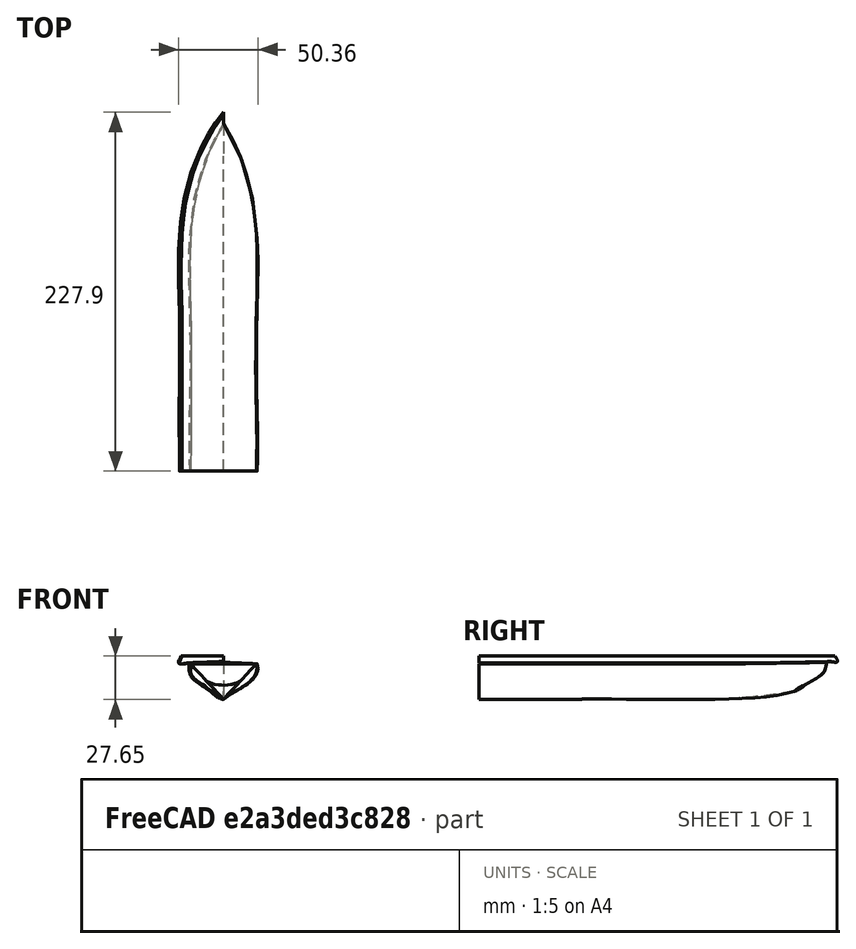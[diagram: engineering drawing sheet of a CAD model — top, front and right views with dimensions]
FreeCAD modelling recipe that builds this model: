
FCSTD DOCUMENT  (FreeCAD 0.21R33771 (Git))
Label: ship drg.
License: All rights reserved
LicenseURL: http://en.wikipedia.org/wiki/All_rights_reserved
objects: Part::FeaturePython×12, App::DocumentObjectGroup×5, Sketcher::SketchObject×4, Part::RuledSurface×3, Part::Loft×2, Part::Mirroring×2, Part::Part2DObjectPython×1, Part::Compound×1
note: 25 computed .brp shape members not serialized (recipe doc carries the construction recipe); baked Part::Feature solids carry a one-line shape summary decoded from their .brp

FEATURE [Sketcher::SketchObject] Sketch
  FullyConstrained = false
  Placement = pos=(0,0,0) rot=(1,0,0;1.5708rad)
  sketch-geometry (14):
    g0: LineSegment StartX=0 StartY=10 StartZ=0 EndX=0 EndY=15.6184 EndZ=0
    g1: LineSegment StartX=0 StartY=15.6184 StartZ=0 EndX=0 EndY=21.2368 EndZ=0
    g2: LineSegment StartX=0 StartY=21.2368 StartZ=0 EndX=0 EndY=26.8551 EndZ=0
    g3: LineSegment StartX=0 StartY=26.8551 StartZ=0 EndX=0 EndY=32.4735 EndZ=0
    g4: LineSegment StartX=0 StartY=32.4735 StartZ=0 EndX=0 EndY=38.0919 EndZ=0
    g5: LineSegment StartX=0 StartY=10 StartZ=0 EndX=0 EndY=0 EndZ=0
    g6: LineSegment StartX=0 StartY=15.6184 StartZ=0 EndX=8.31751 EndY=15.6184 EndZ=0
    g7: LineSegment StartX=0 StartY=21.2368 StartZ=0 EndX=16.635 EndY=21.2368 EndZ=0
    g8: LineSegment StartX=0 StartY=26.8551 StartZ=0 EndX=20.7934 EndY=26.8551 EndZ=0
    g9: LineSegment StartX=0 StartY=32.4735 StartZ=0 EndX=20.9422 EndY=32.4735 EndZ=0
    g10: LineSegment StartX=0 StartY=10 StartZ=0 EndX=16.635 EndY=21.2368 EndZ=0
    g11: Circle CenterX=10.7614 CenterY=29.9321 CenterZ=0 NormalX=0 NormalY=0 NormalZ=1 AngleXU=0 Radius=10.4932
    g12: LineSegment StartX=20.9422 StartY=32.4735 StartZ=0 EndX=26.3293 EndY=32.4735 EndZ=0
    g13: LineSegment StartX=26.3293 StartY=32.4735 StartZ=0 EndX=26.3293 EndY=37.3944 EndZ=0
  constraints (36):
    c: PointOnObject(g0,g-2)
    c: PointOnObject(g0,g-2)
    c: Coincident(g0,g1)
    c: PointOnObject(g1,g-2)
    c: Coincident(g1,g2)
    c: PointOnObject(g2,g-2)
    c: Coincident(g2,g3)
    c: PointOnObject(g3,g-2)
    c: Coincident(g3,g4)
    c: PointOnObject(g4,g-2)
    c: Equal(g4,g3)
    c: Equal(g3,g2)
    c: Equal(g2,g1)
    c: Equal(g1,g0)
    c: Coincident(g5,g0)
    c: Coincident(g5,g-1)
    c: DistanceY(g5,g5) = 10
    c: Coincident(g6,g0)
    c: Horizontal(g6)
    c: Coincident(g7,g1)
    c: Horizontal(g7)
    c: Coincident(g8,g2)
    c: Horizontal(g8)
    c: Coincident(g9,g3)
    c: Horizontal(g9)
    c: Coincident(g10,g0)
    c: Coincident(g10,g7)
    c: PointOnObject(g6,g10)
    c: PointOnObject(g7,g11)
    c: PointOnObject(g8,g11)
    c: PointOnObject(g9,g11)
    c: Tangent(g10,g11)
    c: Coincident(g12,g9)
    c: Horizontal(g12)
    c: Coincident(g13,g12)
    c: Vertical(g13)
FEATURE [Part::FeaturePython] Interpolation_Curve  # WARN: FeaturePython — macro-defined, semantics opaque (R4)
  CustomTangents = false
  DetectAligned = false
  Parameters = [0,0.171956,0.385813,0.692906,1]
  Parametrization = 0
  Periodic = false
  PointList = -> [Sketch]
  Polygonal = false
  StartOffset = 0
  Tangents = (5) [(0.285541,2.128e-16,-0.958366),(-0.349691,2.08026e-16,-0.936865),(-0.74239,1.48763e-16,-0.669969),(-0.866574,1.10811e-16,-0.499049),(-0.736883,1.50107e-16,-0.67602)]
  Tolerance = 1e-07
  UTurns = 0
  VTurns = 0
  WireOutput = false
FEATURE [App::DocumentObjectGroup] Group  label="section1"
  Group = -> [Sketch,Interpolation_Curve]
FEATURE [Sketcher::SketchObject] Sketch001
  FullyConstrained = false
  Placement = pos=(0,50,0) rot=(1,0,0;1.5708rad)
  sketch-geometry (14):
    g0: LineSegment StartX=0 StartY=10 StartZ=0 EndX=0 EndY=15.6184 EndZ=0
    g1: LineSegment StartX=0 StartY=15.6184 StartZ=0 EndX=0 EndY=21.2368 EndZ=0
    g2: LineSegment StartX=0 StartY=21.2368 StartZ=0 EndX=0 EndY=26.8551 EndZ=0
    g3: LineSegment StartX=0 StartY=26.8551 StartZ=0 EndX=0 EndY=32.4735 EndZ=0
    g4: LineSegment StartX=0 StartY=32.4735 StartZ=0 EndX=0 EndY=38.0919 EndZ=0
    g5: LineSegment StartX=0 StartY=10 StartZ=0 EndX=0 EndY=0 EndZ=0
    g6: LineSegment StartX=0 StartY=15.6184 StartZ=0 EndX=8.2623 EndY=15.6184 EndZ=0
    g7: LineSegment StartX=0 StartY=21.2368 StartZ=0 EndX=16.5246 EndY=21.2368 EndZ=0
    g8: LineSegment StartX=0 StartY=26.8551 StartZ=0 EndX=20.6246 EndY=26.8551 EndZ=0
    g9: LineSegment StartX=0 StartY=32.4735 StartZ=0 EndX=20.6915 EndY=32.4735 EndZ=0
    g10: LineSegment StartX=0 StartY=10 StartZ=0 EndX=16.5246 EndY=21.2368 EndZ=0
    g11: Circle CenterX=10.7133 CenterY=29.7827 CenterZ=0 NormalX=0 NormalY=0 NormalZ=1 AngleXU=0 Radius=10.3347
    g12: LineSegment StartX=20.6915 StartY=32.4735 StartZ=0 EndX=26.3293 EndY=32.4735 EndZ=0
    g13: LineSegment StartX=26.3293 StartY=32.4735 StartZ=0 EndX=26.3293 EndY=37.3944 EndZ=0
  constraints (36):
    c: PointOnObject(g0,g-2)
    c: PointOnObject(g0,g-2)
    c: Coincident(g0,g1)
    c: PointOnObject(g1,g-2)
    c: Coincident(g1,g2)
    c: PointOnObject(g2,g-2)
    c: Coincident(g2,g3)
    c: PointOnObject(g3,g-2)
    c: Coincident(g3,g4)
    c: PointOnObject(g4,g-2)
    c: Equal(g4,g3)
    c: Equal(g3,g2)
    c: Equal(g2,g1)
    c: Equal(g1,g0)
    c: Coincident(g5,g0)
    c: Coincident(g5,g-1)
    c: DistanceY(g5,g5) = 10
    c: Coincident(g6,g0)
    c: Horizontal(g6)
    c: Coincident(g7,g1)
    c: Horizontal(g7)
    c: Coincident(g8,g2)
    c: Horizontal(g8)
    c: Coincident(g9,g3)
    c: Horizontal(g9)
    c: Coincident(g10,g0)
    c: Coincident(g10,g7)
    c: PointOnObject(g6,g10)
    c: PointOnObject(g7,g11)
    c: PointOnObject(g8,g11)
    c: PointOnObject(g9,g11)
    c: Tangent(g10,g11)
    c: Coincident(g12,g9)
    c: Horizontal(g12)
    c: Coincident(g13,g12)
    c: Vertical(g13)
FEATURE [Part::FeaturePython] Interpolation_Curve001  # WARN: FeaturePython — macro-defined, semantics opaque (R4)
  CustomTangents = false
  DetectAligned = false
  Parameters = [0,0.172581,0.386214,0.693107,1]
  Parametrization = 0
  Periodic = false
  PointList = -> [Sketch001]
  Polygonal = false
  StartOffset = 0
  Tangents = (5) [(0.285541,2.128e-16,-0.958366),(-0.349691,2.08026e-16,-0.936865),(-0.74239,1.48763e-16,-0.669969),(-0.866574,1.10811e-16,-0.499049),(-0.736883,1.50107e-16,-0.67602)]
  Tolerance = 1e-07
  UTurns = 0
  VTurns = 0
  WireOutput = false
FEATURE [App::DocumentObjectGroup] Group001  label="section002"
  Group = -> [Sketch001,Interpolation_Curve001]
FEATURE [Sketcher::SketchObject] Sketch002
  FullyConstrained = false
  Placement = pos=(0,100,0) rot=(1,0,0;1.5708rad)
  sketch-geometry (14):
    g0: LineSegment StartX=0 StartY=10 StartZ=0 EndX=0 EndY=15.6184 EndZ=0
    g1: LineSegment StartX=0 StartY=15.6184 StartZ=0 EndX=0 EndY=21.2368 EndZ=0
    g2: LineSegment StartX=0 StartY=21.2368 StartZ=0 EndX=0 EndY=26.8551 EndZ=0
    g3: LineSegment StartX=0 StartY=26.8551 StartZ=0 EndX=0 EndY=32.4735 EndZ=0
    g4: LineSegment StartX=0 StartY=32.4735 StartZ=0 EndX=0 EndY=38.0919 EndZ=0
    g5: LineSegment StartX=0 StartY=10 StartZ=0 EndX=0 EndY=0 EndZ=0
    g6: LineSegment StartX=0 StartY=15.6184 StartZ=0 EndX=8.31751 EndY=15.6184 EndZ=0
    g7: LineSegment StartX=0 StartY=21.2368 StartZ=0 EndX=16.635 EndY=21.2368 EndZ=0
    g8: LineSegment StartX=0 StartY=26.8551 StartZ=0 EndX=20.7934 EndY=26.8551 EndZ=0
    g9: LineSegment StartX=0 StartY=32.4735 StartZ=0 EndX=20.9422 EndY=32.4735 EndZ=0
    g10: LineSegment StartX=0 StartY=10 StartZ=0 EndX=16.635 EndY=21.2368 EndZ=0
    g11: Circle CenterX=10.7614 CenterY=29.9321 CenterZ=0 NormalX=0 NormalY=0 NormalZ=1 AngleXU=0 Radius=10.4932
    g12: LineSegment StartX=20.9422 StartY=32.4735 StartZ=0 EndX=26.3293 EndY=32.4735 EndZ=0
    g13: LineSegment StartX=26.3293 StartY=32.4735 StartZ=0 EndX=26.3293 EndY=37.3944 EndZ=0
  constraints (36):
    c: PointOnObject(g0,g-2)
    c: PointOnObject(g0,g-2)
    c: Coincident(g0,g1)
    c: PointOnObject(g1,g-2)
    c: Coincident(g1,g2)
    c: PointOnObject(g2,g-2)
    c: Coincident(g2,g3)
    c: PointOnObject(g3,g-2)
    c: Coincident(g3,g4)
    c: PointOnObject(g4,g-2)
    c: Equal(g4,g3)
    c: Equal(g3,g2)
    c: Equal(g2,g1)
    c: Equal(g1,g0)
    c: Coincident(g5,g0)
    c: Coincident(g5,g-1)
    c: DistanceY(g5,g5) = 10
    c: Coincident(g6,g0)
    c: Horizontal(g6)
    c: Coincident(g7,g1)
    c: Horizontal(g7)
    c: Coincident(g8,g2)
    c: Horizontal(g8)
    c: Coincident(g9,g3)
    c: Horizontal(g9)
    c: Coincident(g10,g0)
    c: Coincident(g10,g7)
    c: PointOnObject(g6,g10)
    c: PointOnObject(g7,g11)
    c: PointOnObject(g8,g11)
    c: PointOnObject(g9,g11)
    c: Tangent(g10,g11)
    c: Coincident(g12,g9)
    c: Horizontal(g12)
    c: Coincident(g13,g12)
    c: Vertical(g13)
FEATURE [Part::FeaturePython] Interpolation_Curve002  # WARN: FeaturePython — macro-defined, semantics opaque (R4)
  CustomTangents = false
  DetectAligned = false
  Parameters = [0,0.171956,0.385813,0.692906,1]
  Parametrization = 0
  Periodic = false
  PointList = -> [Sketch002]
  Polygonal = false
  StartOffset = 0
  Tangents = (5) [(0.285541,2.128e-16,-0.958366),(-0.349691,2.08026e-16,-0.936865),(-0.74239,1.48763e-16,-0.669969),(-0.866574,1.10811e-16,-0.499049),(-0.736883,1.50107e-16,-0.67602)]
  Tolerance = 1e-07
  UTurns = 0
  VTurns = 0
  WireOutput = false
FEATURE [App::DocumentObjectGroup] Group002  label="section003"
  Group = -> [Sketch002,Interpolation_Curve002]
FEATURE [Sketcher::SketchObject] Sketch003
  FullyConstrained = false
  Placement = pos=(0,150,0) rot=(1,0,0;1.5708rad)
  sketch-geometry (14):
    g0: LineSegment StartX=0 StartY=10 StartZ=0 EndX=0 EndY=15.6184 EndZ=0
    g1: LineSegment StartX=0 StartY=15.6184 StartZ=0 EndX=0 EndY=21.2368 EndZ=0
    g2: LineSegment StartX=0 StartY=21.2368 StartZ=0 EndX=0 EndY=26.8551 EndZ=0
    g3: LineSegment StartX=0 StartY=26.8551 StartZ=0 EndX=0 EndY=32.4735 EndZ=0
    g4: LineSegment StartX=0 StartY=32.4735 StartZ=0 EndX=0 EndY=38.0919 EndZ=0
    g5: LineSegment StartX=0 StartY=10 StartZ=0 EndX=0 EndY=0 EndZ=0
    g6: LineSegment StartX=0 StartY=15.6184 StartZ=0 EndX=8.31751 EndY=15.6184 EndZ=0
    g7: LineSegment StartX=0 StartY=21.2368 StartZ=0 EndX=16.635 EndY=21.2368 EndZ=0
    g8: LineSegment StartX=0 StartY=26.8551 StartZ=0 EndX=20.7934 EndY=26.8551 EndZ=0
    g9: LineSegment StartX=0 StartY=32.4735 StartZ=0 EndX=20.9422 EndY=32.4735 EndZ=0
    g10: LineSegment StartX=0 StartY=10 StartZ=0 EndX=16.635 EndY=21.2368 EndZ=0
    g11: Circle CenterX=10.7614 CenterY=29.9321 CenterZ=0 NormalX=0 NormalY=0 NormalZ=1 AngleXU=0 Radius=10.4932
    g12: LineSegment StartX=20.9422 StartY=32.4735 StartZ=0 EndX=26.3293 EndY=32.4735 EndZ=0
    g13: LineSegment StartX=26.3293 StartY=32.4735 StartZ=0 EndX=26.3293 EndY=37.3944 EndZ=0
  constraints (36):
    c: PointOnObject(g0,g-2)
    c: PointOnObject(g0,g-2)
    c: Coincident(g0,g1)
    c: PointOnObject(g1,g-2)
    c: Coincident(g1,g2)
    c: PointOnObject(g2,g-2)
    c: Coincident(g2,g3)
    c: PointOnObject(g3,g-2)
    c: Coincident(g3,g4)
    c: PointOnObject(g4,g-2)
    c: Equal(g4,g3)
    c: Equal(g3,g2)
    c: Equal(g2,g1)
    c: Equal(g1,g0)
    c: Coincident(g5,g0)
    c: Coincident(g5,g-1)
    c: DistanceY(g5,g5) = 10
    c: Coincident(g6,g0)
    c: Horizontal(g6)
    c: Coincident(g7,g1)
    c: Horizontal(g7)
    c: Coincident(g8,g2)
    c: Horizontal(g8)
    c: Coincident(g9,g3)
    c: Horizontal(g9)
    c: Coincident(g10,g0)
    c: Coincident(g10,g7)
    c: PointOnObject(g6,g10)
    c: PointOnObject(g7,g11)
    c: PointOnObject(g8,g11)
    c: PointOnObject(g9,g11)
    c: Tangent(g10,g11)
    c: Coincident(g12,g9)
    c: Horizontal(g12)
    c: Coincident(g13,g12)
    c: Vertical(g13)
FEATURE [Part::FeaturePython] Interpolation_Curve003  # WARN: FeaturePython — macro-defined, semantics opaque (R4)
  CustomTangents = false
  DetectAligned = false
  Parameters = [0,0.171956,0.385813,0.692906,1]
  Parametrization = 0
  Periodic = false
  PointList = -> [Sketch003]
  Polygonal = false
  StartOffset = 0
  Tangents = (5) [(0.285541,2.128e-16,-0.958366),(-0.349691,2.08026e-16,-0.936865),(-0.74239,1.48763e-16,-0.669969),(-0.866574,1.10811e-16,-0.499049),(-0.736883,1.50107e-16,-0.67602)]
  Tolerance = 1e-07
  UTurns = 0
  VTurns = 0
  WireOutput = false
FEATURE [App::DocumentObjectGroup] Group003  label="section004"
  Group = -> [Sketch003,Interpolation_Curve003]
FEATURE [App::DocumentObjectGroup] Group004  label="section005"
FEATURE [Part::Part2DObjectPython] Clone2D  label="Sketch004 (2D)"  # Draft 2D object (typed FeaturePython)
  Fuse = false
  Placement = pos=(0,200,0) rot=(0.57735,0.57735,0.57735;2.0944rad)
  Scale = (1,1,1)
FEATURE [Part::FeaturePython] Interpolation_Curve005  # WARN: FeaturePython — macro-defined, semantics opaque (R4)
  CustomTangents = false
  DetectAligned = false
  Parameters = [0,0.160768,0.372543,0.686271,1]
  Parametrization = 0
  Periodic = false
  PointList = -> [Clone2D]
  Polygonal = false
  StartOffset = 0
  Tangents = (5) [(2.2067e-16,0.111092,-0.99381),(1.98675e-16,-0.446566,-0.894751),(1.35979e-16,-0.790551,-0.612396),(9.89648e-17,-0.895183,-0.445698),(1.37884e-16,-0.783832,-0.620973)]
  Tolerance = 1e-07
  UTurns = 0
  VTurns = 0
  WireOutput = false
FEATURE [Part::FeaturePython] Interpolation_Curve006  # WARN: FeaturePython — macro-defined, semantics opaque (R4)
  CustomTangents = false
  DetectAligned = false
  Parameters = [0,0.349926,0.566617,0.783309,1]
  Parametrization = 0
  Periodic = false
  PointList = -> [Clone2D,Sketch003,Sketch002,Sketch001,Sketch]
  Polygonal = false
  StartOffset = 0
  Tangents = (5) [(0.604457,-0.796638,0),(0.0641319,-0.997941,7.34674e-17),(-0.016904,-0.999857,-8.28925e-17),(0.00424159,-0.999991,-3.55521e-17),(0,-1,0)]
  Tolerance = 1e-07
  UTurns = 0
  VTurns = 0
  WireOutput = false
FEATURE [Part::FeaturePython] Interpolation_Curve007  # WARN: FeaturePython — macro-defined, semantics opaque (R4)
  CustomTangents = false
  DetectAligned = false
  Parameters = [0,0.349943,0.566629,0.783314,1]
  Parametrization = 0
  Periodic = false
  PointList = -> [Clone2D,Sketch003,Sketch002,Sketch001,Sketch]
  Polygonal = false
  StartOffset = 0
  Tangents = (5) [(0.60434,-0.796395,-0.0229786),(0.0641222,-0.997939,-0.00243809),(-0.0169012,-0.999857,0.000642627),(0.00424091,-0.999991,-0.00016125),(-1.44342e-18,-1,2.25534e-20)]
  Tolerance = 1e-07
  UTurns = 0
  VTurns = 0
  WireOutput = false
FEATURE [Part::FeaturePython] Interpolation_Curve008  # WARN: FeaturePython — macro-defined, semantics opaque (R4)
  CustomTangents = false
  DetectAligned = false
  Parameters = [0,0.329578,0.55305,0.776525,1]
  Parametrization = 0
  Periodic = false
  PointList = -> [Clone2D,Sketch003,Sketch002,Sketch001,Sketch]
  Polygonal = false
  StartOffset = 0
  Tangents = (5) [(0.530424,-0.847354,-0.025356),(0.0614918,-0.998103,-0.00293951),(-0.0162426,-0.999868,0.00077645),(0.00407317,-0.999992,-0.000194711),(2.97726e-18,-1,-4.65197e-20)]
  Tolerance = 1e-07
  UTurns = 0
  VTurns = 0
  WireOutput = false
FEATURE [Part::FeaturePython] Interpolation_Curve009  # WARN: FeaturePython — macro-defined, semantics opaque (R4)
  CustomTangents = false
  DetectAligned = false
  Parameters = [0,0.327197,0.551464,0.775732,1]
  Parametrization = 0
  Periodic = false
  PointList = -> [Clone2D,Sketch003,Sketch002,Sketch001,Sketch]
  Polygonal = false
  StartOffset = 0
  Tangents = (5) [(0.530727,-0.846003,-0.0510689),(0.0624343,-0.998031,-0.0060077),(-0.0164877,-0.999863,0.00158652),(0.00413499,-0.999991,-0.000397887),(0,-1,2.33425e-19)]
  Tolerance = 1e-07
  UTurns = 0
  VTurns = 0
  WireOutput = false
FEATURE [Part::FeaturePython] Interpolation_Curve010  # WARN: FeaturePython — macro-defined, semantics opaque (R4)
  CustomTangents = false
  DetectAligned = false
  Parameters = [0,0.311707,0.541138,0.770569,1]
  Parametrization = 0
  Periodic = false
  PointList = -> [Clone2D,Sketch003,Sketch002,Sketch001,Sketch]
  Polygonal = false
  StartOffset = 0
  Tangents = (5) [(0.457838,-0.885192,-0.0825829),(0.0576515,-0.998283,-0.0103989),(-0.015255,-0.99988,0.00275163),(0.00382354,-0.999992,-0.000689675),(-1.52832e-18,-1,-2.13296e-16)]
  Tolerance = 1e-07
  UTurns = 0
  VTurns = 0
  WireOutput = false
FEATURE [Part::FeaturePython] Interpolation_Curve011  # WARN: FeaturePython — macro-defined, semantics opaque (R4)
  CustomTangents = false
  DetectAligned = false
  Parameters = [0,0.281017,0.520678,0.760339,1]
  Parametrization = 0
  Periodic = false
  PointList = -> [Clone2D,Sketch003,Sketch002,Sketch001,Sketch]
  Polygonal = false
  StartOffset = 0
  Tangents = (5) [(0.265192,-0.955723,-0.127543),(0.0384675,-0.999089,-0.0185008),(-0.0102229,-0.999936,0.00491666),(0.00255875,-0.999996,-0.00123062),(1.06564e-16,-1,1.06763e-16)]
  Tolerance = 1e-07
  UTurns = 0
  VTurns = 0
  WireOutput = false
FEATURE [Part::FeaturePython] Interpolation_Curve012  # WARN: FeaturePython — macro-defined, semantics opaque (R4)
  CustomTangents = false
  DetectAligned = false
  Parameters = [0,0.250934,0.500623,0.750311,1]
  Parametrization = 0
  Periodic = false
  PointList = -> [Clone2D,Sketch003,Sketch002,Sketch001,Sketch]
  Polygonal = false
  StartOffset = 0
  Tangents = (5) [(1.20758e-16,-0.983431,-0.181282),(2.06459e-17,-0.99952,-0.0309936),(-5.49725e-18,-0.999966,0.00825247),(1.37506e-18,-0.999998,-0.00206425),(3.69318e-34,-1,-1.24745e-18)]
  Tolerance = 1e-07
  UTurns = 0
  VTurns = 0
  WireOutput = false
FEATURE [Part::Loft] Loft
  Closed = false
  MaxDegree = 5
  Ruled = false
  Sections = -> [Interpolation_Curve,Interpolation_Curve001,Interpolation_Curve002,Interpolation_Curve003,Interpolation_Curve005]
  Solid = false
FEATURE [Part::Loft] Loft001
  Closed = false
  MaxDegree = 5
  Ruled = false
  Sections = -> [Interpolation_Curve006,Interpolation_Curve007,Interpolation_Curve008,Interpolation_Curve009,Interpolation_Curve010,Interpolation_Curve011,Interpolation_Curve012]
  Solid = false
FEATURE [Part::Mirroring] Part__Mirroring  label="Loft (Mirror #1)"
  Base = (0,0,0)
  Normal = (1,0,0)
  Source = -> Loft
FEATURE [Part::Mirroring] Part__Mirroring001  label="Loft001 (Mirror #2)"
  Base = (0,0,0)
  Normal = (1,0,0)
  Source = -> Loft001
FEATURE [Part::RuledSurface] Ruled_Surface
  Curve1 = -> Loft [Edge4]
  Curve2 = -> Part__Mirroring [Edge4]
  Orientation = 0
FEATURE [Part::RuledSurface] Ruled_Surface001
  Curve1 = -> Ruled_Surface [Edge2]
  Curve2 = -> Interpolation_Curve [Edge1]
  Orientation = 0
FEATURE [Part::RuledSurface] Ruled_Surface002
  Curve1 = -> Interpolation_Curve [Edge1]
  Curve2 = -> Part__Mirroring [Edge1]
  Orientation = 0
FEATURE [Part::Compound] Compound
  Links = -> [Ruled_Surface002,Part__Mirroring,Loft,Ruled_Surface,Ruled_Surface001,Part__Mirroring001]
